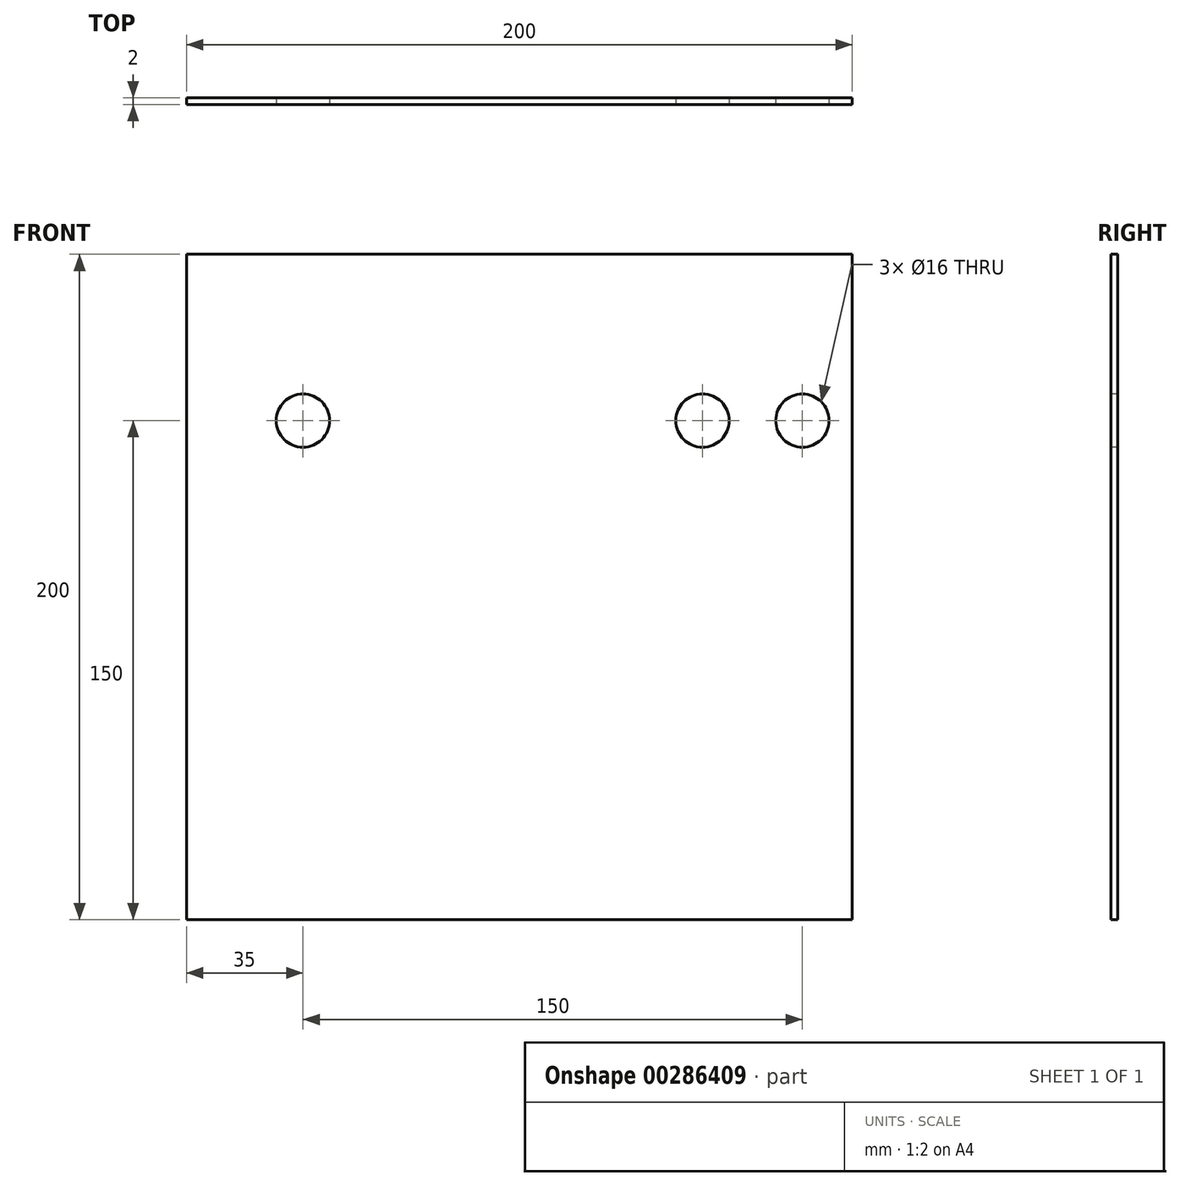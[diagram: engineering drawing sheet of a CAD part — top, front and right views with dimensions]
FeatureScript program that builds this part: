
annotation { "Feature Type Name" : "Feature", "Feature Type Description" : "" }
export const myFeature = defineFeature(function(context is Context, id is Id, definition is map)
    precondition{}
    {
        {
            var Q0;
            Q0=qCreatedBy(makeId("Front.planeOp"),FACE);
            var sketch = newSketch(context, id + "F0", { "sketchPlane" : qUnion([Q0])});
            skLineSegment(sketch, "E0.bottom", {"start": v(0, 200) * mm, "end": v(200, 200) * mm});
            skLineSegment(sketch, "E0.top", {"start": v(0, 0) * mm, "end": v(200, 0) * mm});
            skLineSegment(sketch, "E0.left", {"start": v(0, 200) * mm, "end": v(0, 0) * mm});
            skLineSegment(sketch, "E0.right", {"start": v(200, 200) * mm, "end": v(200, 0) * mm});
            skSolve(sketch);
        }
        {
            var Q0;
            Q0 = qSketchRegion(id + "F0", true);
            extrude(context, id + "F1", {"entities" : qUnion([Q0]), "oppositeDirection" : true, "depth" : 2 * mm});
        }
        {
            var Q0;
            Q0=makeQuery(id+"F1.opExtrude","CAP_FACE",FACE,{"disambiguationData":[OSD([sQuery(id+"F0.wireOp",EDGE,"E0.bottom"),sQuery(id+"F0.wireOp",EDGE,"E0.top"),sQuery(id+"F0.wireOp",EDGE,"E0.left"),sQuery(id+"F0.wireOp",EDGE,"E0.right")])],"isStart":true});
            var sketch = newSketch(context, id + "F2", { "sketchPlane" : qUnion([Q0])});
            skCircle(sketch, "E1", {"center": v(35, 150) * mm, "radius": 8 * mm});
            skCircle(sketch, "E2", {"center": v(155, 150) * mm, "radius": 8 * mm});
            skCircle(sketch, "E3", {"center": v(185, 150) * mm, "radius": 8 * mm});
            skSolve(sketch);
        }
        {
            var Q0;
            Q0 = qSketchRegion(id + "F2", true);
            extrude(context, id + "F3", {"entities" : qUnion([Q0]), "operationType" : NewBodyOperationType.REMOVE, "endBound" : BoundingType.UP_TO_NEXT, "oppositeDirection" : true, "depth" : 25 * mm});
        }
    });
